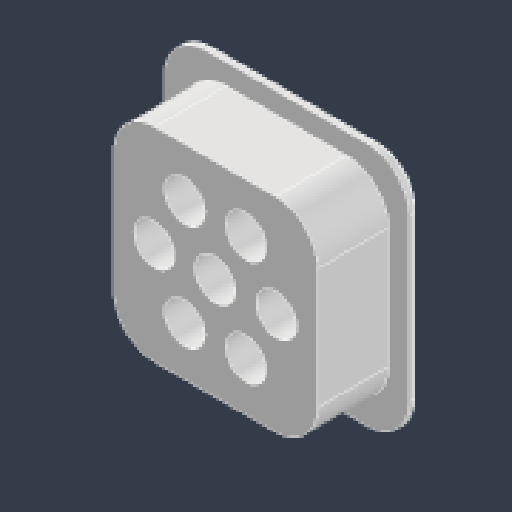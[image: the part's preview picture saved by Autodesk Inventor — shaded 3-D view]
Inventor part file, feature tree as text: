
AUTODESK INVENTOR PART (.ipt)
format: ipt  version: 2023.4 (Build 274418000, 418)  size: 156,160 bytes
history: native  units: mm
features: extrude x3, sketch x3, fillet x1, chamfer x1, pattern_circular x1
ambient origin geometry x8: Origin, YZ Plane, XZ Plane, XY Plane, X Axis, Y Axis, Z Axis, Center Point
bodies: Solid1 (feature_tree)
feature tree (9):
  extrude  "Extrusion1"  Depth=24.0mm
  extrude  "Extrusion2"  Depth=20.0mm
  fillet  "Fillet1"  Radius=20.0mm
  chamfer  "Chamfer1"  Distance=7.0mm
  extrude  "Extrusion3"  Depth=2.0mm TaperAngle=45.0deg
  pattern_circular  "Circular Pattern1"  [2 undecoded]
  sketch  "Sketch1"  dims[d0=24.0mm d1=24.0mm]
  sketch  "Sketch2"  dims[d2=1.0mm d3=0.0mm d4=20.0mm d5=20.0mm d6=7.0mm d7=0.0mm]
  sketch  "Sketch3"  dims[d8=4.1mm d9=0.4mm d10=2.0mm d11=45.0deg d12=5.0mm d13=0.0mm d14=0.0mm d15=7.0mm d16=60.0mm d17=360.0deg]
note: 2 required parameter values undecoded (feature->parameter linkage not recoverable at this tier; creation-order binding heuristic only, values carry confidence <= 0.55)
